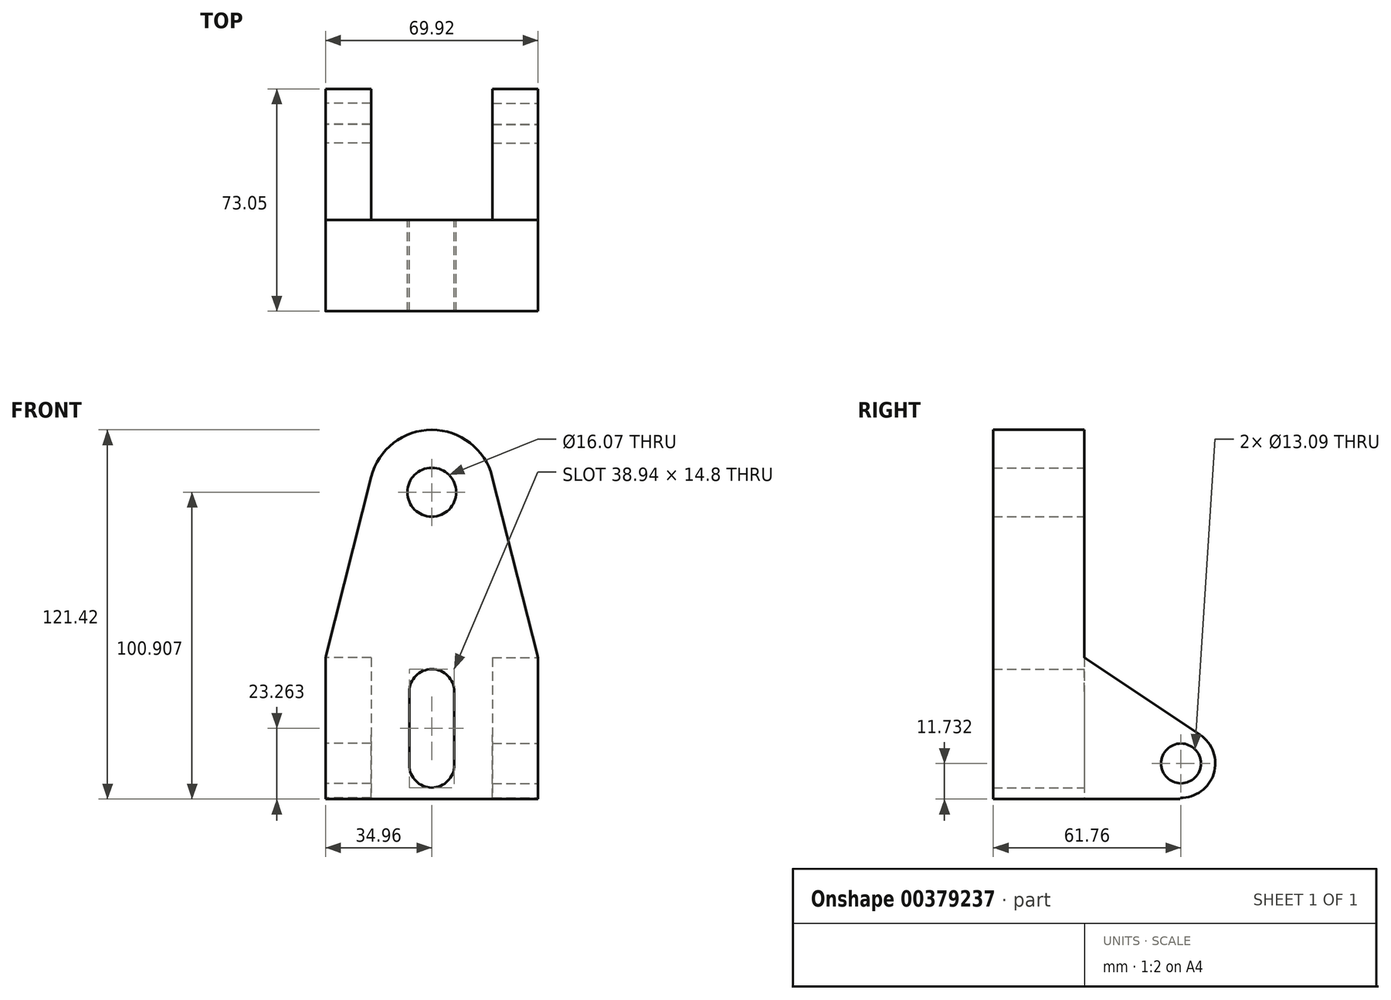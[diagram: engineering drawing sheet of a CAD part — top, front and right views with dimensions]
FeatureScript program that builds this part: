
annotation { "Feature Type Name" : "Feature", "Feature Type Description" : "" }
export const myFeature = defineFeature(function(context is Context, id is Id, definition is map)
    precondition{}
    {
        {
            var Q0;
            Q0=qCreatedBy(makeId("Front.planeOp"),FACE);
            var sketch = newSketch(context, id + "F0", { "sketchPlane" : qUnion([Q0])});
            skLineSegment(sketch, "E0.top", {"start": v(34.96, -60.54) * mm, "end": v(-34.96, -60.54) * mm});
            skLineSegment(sketch, "E0.left", {"start": v(34.96, -14.01) * mm, "end": v(34.96, -60.54) * mm});
            skLineSegment(sketch, "E0.right", {"start": v(-34.96, -14.01) * mm, "end": v(-34.96, -60.54) * mm});
            skPoint(sketch, "E0.middle", {"position": v(0, -37.28) * mm});
            skArc(sketch, "E1", {"start": v(19.89, 45.41) * mm, "mid": v(0, 60.88) * mm, "end": v(-19.89, 45.41) * mm});
            skLineSegment(sketch, "E2", {"start": v(-34.96, -14.01) * mm, "end": v(-19.89, 45.41) * mm});
            skLineSegment(sketch, "E3", {"start": v(34.96, -14.01) * mm, "end": v(19.89, 45.41) * mm});
            skCircle(sketch, "E4", {"center": v(0, 40.37) * mm, "radius": 8.03 * mm});
            skLineSegment(sketch, "E5.left", {"start": v(7.4, -25.2) * mm, "end": v(7.4, -49.35) * mm});
            skLineSegment(sketch, "E5.right", {"start": v(-7.4, -25.2) * mm, "end": v(-7.4, -49.35) * mm});
            skArc(sketch, "E6", {"start": v(7.4, -25.2) * mm, "mid": v(0, -17.8) * mm, "end": v(-7.4, -25.2) * mm});
            skArc(sketch, "E7", {"start": v(-7.4, -49.35) * mm, "mid": v(0, -56.75) * mm, "end": v(7.4, -49.35) * mm});
            skSolve(sketch);
        }
        {
            var Q0;
            Q0=makeQuery(id+"F0.imprint","IMPRINT",FACE,{"disambiguationData":[TD([[makeQuery(id+"F0.imprint","IMPRINT",EDGE,{"derivedFrom":sQuery(id+"F0.wireOp",EDGE,"E0.top")}),-1.0]])]});
            extrude(context, id + "F1", {"entities" : qUnion([Q0]), "endBound" : BoundingType.SYMMETRIC, "depth" : 30 * mm, "offsetDistance" : 25.4 * mm});
        }
        {
            var Q0;
            Q0=makeQuery(id+"F1.opExtrude","SWEPT_FACE",FACE,{"disambiguationData":[OSD([sQuery(id+"F0.wireOp",EDGE,"E0.left")])]});
            var sketch = newSketch(context, id + "F2", { "sketchPlane" : qUnion([Q0])});
            skLineSegment(sketch, "E8", {"start": v(15, -14.01) * mm, "end": v(15, -60.54) * mm});
            skLineSegment(sketch, "E9", {"start": v(15, -60.54) * mm, "end": v(46.4, -60.54) * mm});
            skArc(sketch, "E10", {"start": v(46.55, -60.1) * mm, "mid": v(57.54, -52.19) * mm, "end": v(53.03, -39.42) * mm});
            skLineSegment(sketch, "E11", {"start": v(15, -14.01) * mm, "end": v(53.03, -39.42) * mm});
            skLineSegment(sketch, "E12", {"start": v(46.55, -60.1) * mm, "end": v(46.4, -60.54) * mm});
            skCircle(sketch, "E13", {"center": v(46.76, -48.8) * mm, "radius": 6.54 * mm});
            skSolve(sketch);
        }
        {
            var Q0;
            Q0=makeQuery(id+"F2.imprint","IMPRINT",FACE,{"disambiguationData":[TD([[makeQuery(id+"F2.imprint","IMPRINT",EDGE,{"derivedFrom":sQuery(id+"F2.wireOp",EDGE,"E8")}),1.0]])]});
            extrude(context, id + "F3", {"entities" : qUnion([Q0]), "operationType" : NewBodyOperationType.ADD, "oppositeDirection" : true, "depth" : 15 * mm, "offsetDistance" : 25.4 * mm});
        }
        {
            var Q0;
            Q0=makeQuery(id+"F3.opExtrude","CAP_EDGE",EDGE,{"disambiguationData":[OSD([sQuery(id+"F2.wireOp",EDGE,"E8")])],"isStart":false});
            var Q1;
            Q1=makeQuery(id+"F1.opExtrude","SWEPT_EDGE",EDGE,{"disambiguationData":[OSD([sQuery(id+"F0.wireOp",EDGE,"E0.right"),sQuery(id+"F0.wireOp",EDGE,"E2")])]});
            var Q2;
            Q2=makeQuery(id+"F1.opExtrude","SWEPT_EDGE",EDGE,{"disambiguationData":[OSD([sQuery(id+"F0.wireOp",EDGE,"E0.left"),sQuery(id+"F0.wireOp",EDGE,"E3")])]});
            fillet(context, id + "F4", {"entities" : qUnion([Q0, Q1, Q2]), "radius" : 5.08 * mm, "tangentPropagation" : true, "allowEdgeOverflow" : false});
        }
        {
            var Q0;
            Q0=makeQuery(id+"F1.opExtrude","SWEPT_BODY",BODY,{"disambiguationData":[OSD([sQuery(id+"F0.wireOp",EDGE,"E0.top"),sQuery(id+"F0.wireOp",EDGE,"E0.left"),sQuery(id+"F0.wireOp",EDGE,"E0.right"),sQuery(id+"F0.wireOp",EDGE,"E1"),sQuery(id+"F0.wireOp",EDGE,"E2"),sQuery(id+"F0.wireOp",EDGE,"E3"),sQuery(id+"F0.wireOp",EDGE,"E4"),sQuery(id+"F0.wireOp",EDGE,"E5.left"),sQuery(id+"F0.wireOp",EDGE,"E5.right"),sQuery(id+"F0.wireOp",EDGE,"E6"),sQuery(id+"F0.wireOp",EDGE,"E7")])]});
            var Q1;
            Q1=qCreatedBy(makeId("Right.planeOp"),FACE);
            mirror(context, id + "F5", {"operationType" : NewBodyOperationType.ADD, "entities" : qUnion([Q0]), "mirrorPlane" : qUnion([Q1])});
        }
    });
